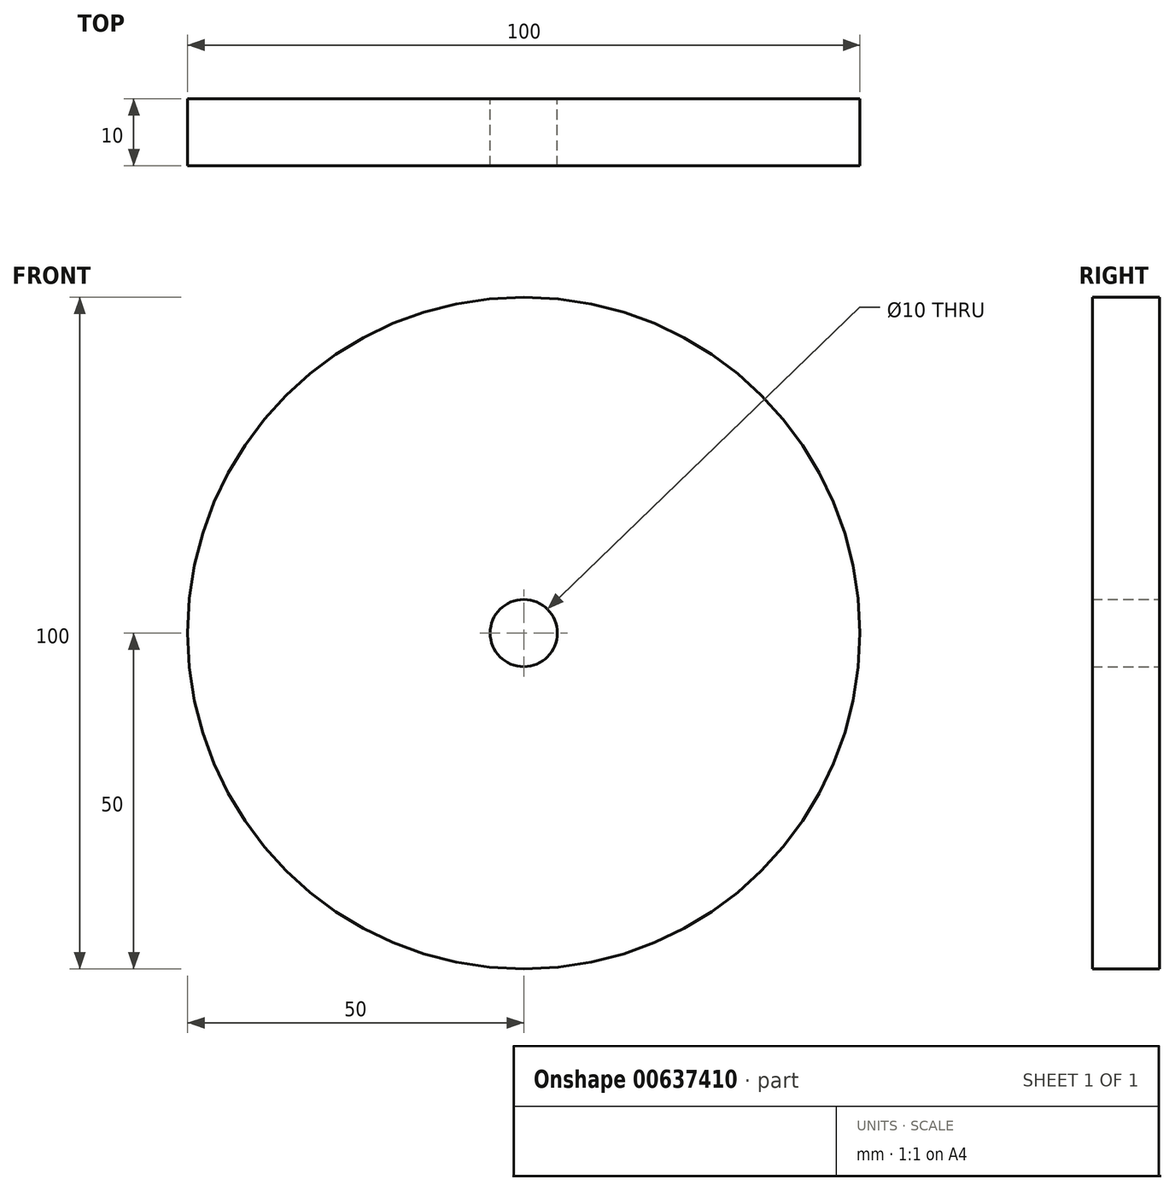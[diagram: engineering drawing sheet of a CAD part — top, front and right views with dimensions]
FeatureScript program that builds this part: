
annotation { "Feature Type Name" : "Feature", "Feature Type Description" : "" }
export const myFeature = defineFeature(function(context is Context, id is Id, definition is map)
    precondition{}
    {
        {
            var Q0;
            Q0=qCreatedBy(makeId("Front.planeOp"),FACE);
            var sketch = newSketch(context, id + "F0", { "sketchPlane" : qUnion([Q0])});
            skCircle(sketch, "E0", {"center": v(0, 0) * mm, "radius": 50 * mm});
            skCircle(sketch, "E1", {"center": v(0, 0) * mm, "radius": 17.5 * mm});
            skCircle(sketch, "E2", {"center": v(0, 0) * mm, "radius": 5 * mm});
            skSolve(sketch);
        }
        {
            var Q0;
            Q0=makeQuery(id+"F0.imprint","IMPRINT",FACE,{"disambiguationData":[TD([[makeQuery(id+"F0.imprint","IMPRINT",EDGE,{"derivedFrom":sQuery(id+"F0.wireOp",EDGE,"E0")}),1.0]])]});
            var Q1;
            Q1=makeQuery(id+"F0.imprint","IMPRINT",FACE,{"disambiguationData":[TD([[makeQuery(id+"F0.imprint","IMPRINT",EDGE,{"derivedFrom":sQuery(id+"F0.wireOp",EDGE,"E1")}),1.0]])]});
            extrude(context, id + "F1", {"entities" : qUnion([Q0, Q1]), "depth" : 10 * mm, "offsetDistance" : 25 * mm});
        }
    });
